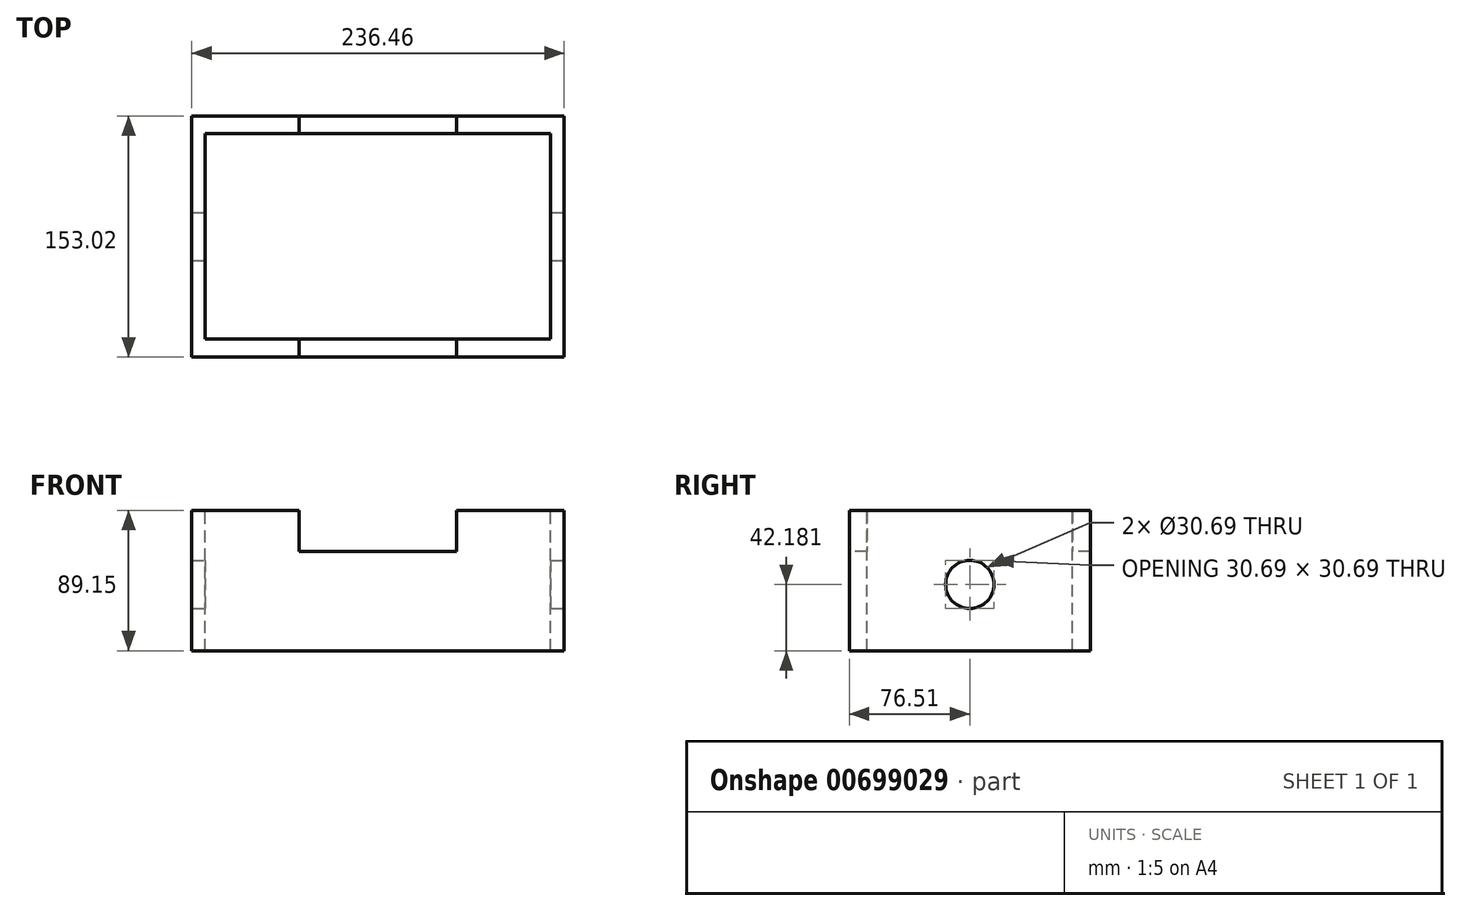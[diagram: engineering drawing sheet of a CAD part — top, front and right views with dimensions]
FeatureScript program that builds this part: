
annotation { "Feature Type Name" : "Feature", "Feature Type Description" : "" }
export const myFeature = defineFeature(function(context is Context, id is Id, definition is map)
    precondition{}
    {
        {
            var Q0;
            Q0=qCreatedBy(makeId("Top.planeOp"),FACE);
            var sketch = newSketch(context, id + "F0", { "sketchPlane" : qUnion([Q0])});
            skLineSegment(sketch, "E0.bottom", {"start": v(118.23, 76.5) * mm, "end": v(-118.23, 76.5) * mm});
            skLineSegment(sketch, "E0.top", {"start": v(118.23, -76.5) * mm, "end": v(-118.23, -76.5) * mm});
            skLineSegment(sketch, "E0.left", {"start": v(118.23, 76.5) * mm, "end": v(118.23, -76.5) * mm});
            skLineSegment(sketch, "E0.right", {"start": v(-118.23, 76.5) * mm, "end": v(-118.23, -76.5) * mm});
            skPoint(sketch, "E0.middle", {"position": v(0, 0) * mm});
            skSolve(sketch);
        }
        {
            var Q0;
            Q0 = qSketchRegion(id + "F0", true);
            extrude(context, id + "F1", {"entities" : qUnion([Q0]), "depth" : 89.15 * mm, "offsetDistance" : 25.4 * mm});
        }
        {
            var Q0;
            Q0=makeQuery(id+"F1.opExtrude","CAP_FACE",FACE,{"disambiguationData":[OSD([sQuery(id+"F0.wireOp",EDGE,"E0.bottom"),sQuery(id+"F0.wireOp",EDGE,"E0.top"),sQuery(id+"F0.wireOp",EDGE,"E0.left"),sQuery(id+"F0.wireOp",EDGE,"E0.right")])],"isStart":false});
            var sketch = newSketch(context, id + "F2", { "sketchPlane" : qUnion([Q0])});
            skLineSegment(sketch, "E1.bottom", {"start": v(109.7, 65.25) * mm, "end": v(-109.7, 65.25) * mm});
            skLineSegment(sketch, "E1.top", {"start": v(109.7, -65.25) * mm, "end": v(-109.7, -65.25) * mm});
            skLineSegment(sketch, "E1.left", {"start": v(109.7, 65.25) * mm, "end": v(109.7, -65.25) * mm});
            skLineSegment(sketch, "E1.right", {"start": v(-109.7, 65.25) * mm, "end": v(-109.7, -65.25) * mm});
            skPoint(sketch, "E1.middle", {"position": v(0, 0) * mm});
            skSolve(sketch);
        }
        {
            var Q0;
            Q0 = qSketchRegion(id + "F2", true);
            extrude(context, id + "F3", {"entities" : qUnion([Q0]), "operationType" : NewBodyOperationType.REMOVE, "oppositeDirection" : true, "depth" : 170.43 * mm, "offsetDistance" : 25.4 * mm});
        }
        {
            var Q0;
            Q0=makeQuery(id+"F1.opExtrude","SWEPT_FACE",FACE,{"disambiguationData":[OSD([sQuery(id+"F0.wireOp",EDGE,"E0.top")])]});
            var sketch = newSketch(context, id + "F4", { "sketchPlane" : qUnion([Q0])});
            skLineSegment(sketch, "E2.bottom", {"start": v(49.98, 63.18) * mm, "end": v(-49.98, 63.18) * mm});
            skLineSegment(sketch, "E2.top", {"start": v(49.98, 115.12) * mm, "end": v(-49.98, 115.12) * mm});
            skLineSegment(sketch, "E2.left", {"start": v(49.98, 63.18) * mm, "end": v(49.98, 115.12) * mm});
            skLineSegment(sketch, "E2.right", {"start": v(-49.98, 63.18) * mm, "end": v(-49.98, 115.12) * mm});
            skPoint(sketch, "E2.middle", {"position": v(0, 89.15) * mm});
            skSolve(sketch);
        }
        {
            var Q0;
            Q0 = qSketchRegion(id + "F4", true);
            extrude(context, id + "F5", {"entities" : qUnion([Q0]), "operationType" : NewBodyOperationType.REMOVE, "oppositeDirection" : true, "depth" : 169.93 * mm, "offsetDistance" : 25.4 * mm});
        }
        {
            var Q0;
            Q0=makeQuery(id+"F1.opExtrude","SWEPT_FACE",FACE,{"disambiguationData":[OSD([sQuery(id+"F0.wireOp",EDGE,"E0.left")])]});
            var sketch = newSketch(context, id + "F6", { "sketchPlane" : qUnion([Q0])});
            skCircle(sketch, "E3", {"center": v(0, 42.18) * mm, "radius": 15.35 * mm});
            skSolve(sketch);
        }
        {
            var Q0;
            Q0 = qSketchRegion(id + "F6", true);
            extrude(context, id + "F7", {"entities" : qUnion([Q0]), "operationType" : NewBodyOperationType.REMOVE, "oppositeDirection" : true, "depth" : 355.85 * mm, "offsetDistance" : 25.4 * mm});
        }
    });
